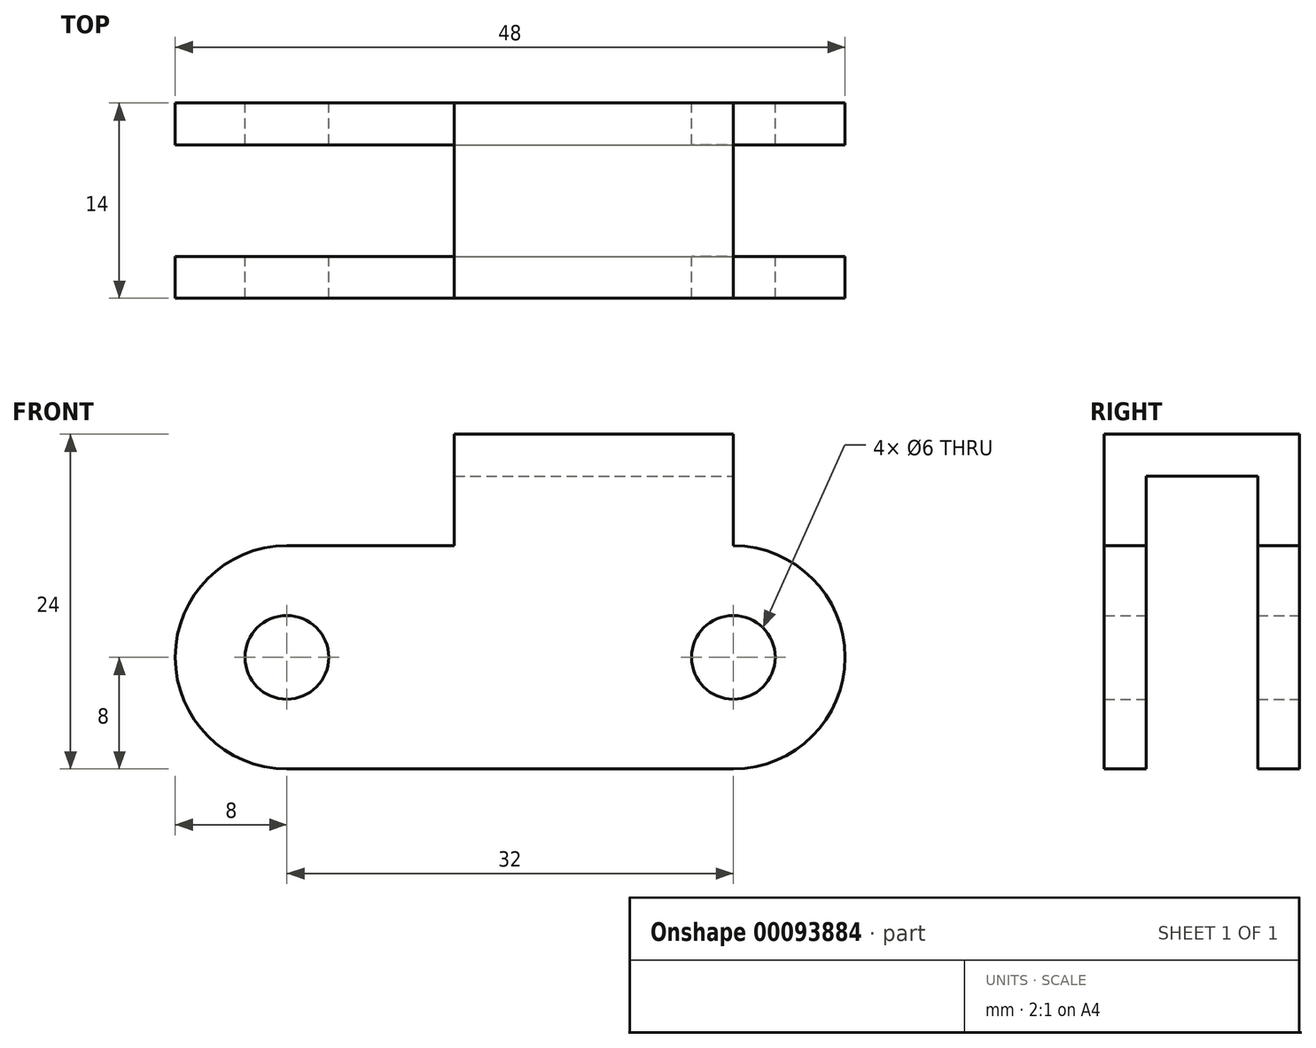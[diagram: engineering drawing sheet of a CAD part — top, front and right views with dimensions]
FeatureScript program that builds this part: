
annotation { "Feature Type Name" : "Feature", "Feature Type Description" : "" }
export const myFeature = defineFeature(function(context is Context, id is Id, definition is map)
    precondition{}
    {
        {
            var Q0;
            Q0=qCreatedBy(makeId("Front.planeOp"),FACE);
            var sketch = newSketch(context, id + "F0", { "sketchPlane" : qUnion([Q0])});
            skLineSegment(sketch, "E0", {"start": v(-16, 0) * mm, "end": v(16, 0) * mm, "construction": true});
            skArc(sketch, "E1.0.startCap", {"start": v(-16, -8) * mm, "mid": v(-24, 0) * mm, "end": v(-16, 8) * mm});
            skArc(sketch, "E1.0.endCap", {"start": v(16, 8) * mm, "mid": v(24, 0) * mm, "end": v(16, -8) * mm});
            skLineSegment(sketch, "E1.0.left", {"start": v(-16, 8) * mm, "end": v(-4, 8) * mm});
            skLineSegment(sketch, "E1.0.right", {"start": v(-16, -8) * mm, "end": v(16, -8) * mm});
            skCircle(sketch, "E2", {"center": v(-16, 0) * mm, "radius": 3 * mm});
            skCircle(sketch, "E3", {"center": v(16, 0) * mm, "radius": 3 * mm});
            skLineSegment(sketch, "E4", {"start": v(16, 8) * mm, "end": v(16, 16) * mm});
            skPoint(sketch, "E5", {"position": v(-4, 8) * mm});
            skLineSegment(sketch, "E6", {"start": v(-4, 8) * mm, "end": v(-4, 16) * mm});
            skLineSegment(sketch, "E7", {"start": v(-4, 16) * mm, "end": v(16, 16) * mm});
            skSolve(sketch);
        }
        {
            var Q0;
            Q0 = qSketchRegion(id + "F0", true);
            extrude(context, id + "F1", {"entities" : qUnion([Q0]), "depth" : 14 * mm});
        }
        {
            var Q0;
            Q0=makeQuery(id+"F1.opExtrude","SWEPT_FACE",FACE,{"disambiguationData":[OSD([sQuery(id+"F0.wireOp",EDGE,"E1.0.endCap")])]});
            var Q1;
            Q1=makeQuery(id+"F1.opExtrude","SWEPT_FACE",FACE,{"disambiguationData":[OSD([sQuery(id+"F0.wireOp",EDGE,"E4")])]});
            var Q2;
            Q2=makeQuery(id+"F1.opExtrude","SWEPT_FACE",FACE,{"disambiguationData":[OSD([sQuery(id+"F0.wireOp",EDGE,"E6")])]});
            var Q3;
            Q3=makeQuery(id+"F1.opExtrude","SWEPT_FACE",FACE,{"disambiguationData":[OSD([sQuery(id+"F0.wireOp",EDGE,"E1.0.startCap")])]});
            var Q4;
            Q4=makeQuery(id+"F1.opExtrude","SWEPT_FACE",FACE,{"disambiguationData":[OSD([sQuery(id+"F0.wireOp",EDGE,"E1.0.left")])]});
            var Q5;
            Q5=makeQuery(id+"F1.opExtrude","SWEPT_FACE",FACE,{"disambiguationData":[OSD([sQuery(id+"F0.wireOp",EDGE,"E1.0.right")])]});
            var Q6;
            Q6=makeQuery(id+"F1.opExtrude","SWEPT_FACE",FACE,{"disambiguationData":[OSD([sQuery(id+"F0.wireOp",EDGE,"E3")])]});
            var Q7;
            Q7=makeQuery(id+"F1.opExtrude","SWEPT_FACE",FACE,{"disambiguationData":[OSD([sQuery(id+"F0.wireOp",EDGE,"E2")])]});
            shell(context, id + "F2", {"entities" : qUnion([Q0, Q1, Q2, Q3, Q4, Q5, Q6, Q7]), "thickness" : 3 * mm});
        }
    });
